# Revit family: 400 Wide - High Stools
name_source: partatom
category: Furniture
units: mm (PartAtom-declared; Revit-internal decimal feet)

## family parameters
Always vertical = Yes
Cut with Voids When Loaded = No
OmniClass Number = 23.40.20.00
OmniClass Title = General Furniture and Specialties
Room Calculation Point = No
Shared = No
Work Plane-Based = No

## types (1)
- GD2B1
    A-Code = No
    Assembly Code = E2020200
    B-Code = Yes
    Crossrail = Gresham - BLACK METAL
    Feet = Gresham - BLACK PLASTIC
    Legs = Gresham - ASH
    Manufacturer = Gresham Office Furniture
    Model = GD2
    Product Brochure = https://gof.co.uk
    Product Code = GD2B1
    Product Data Specification = https://gof.co.uk
    Range = SEATING
    Seat Base = Gresham - Camira Halcyon Aspen
    Seat Pad = Gresham - Camira Halcyon Aspen
    Seat Pad (Vis) = Yes
    URL = www.gof.co.uk

## geometry (parser evidence)
native form markers: Blend x2, Sweep x3
no freeform markers — native parametric forms only
